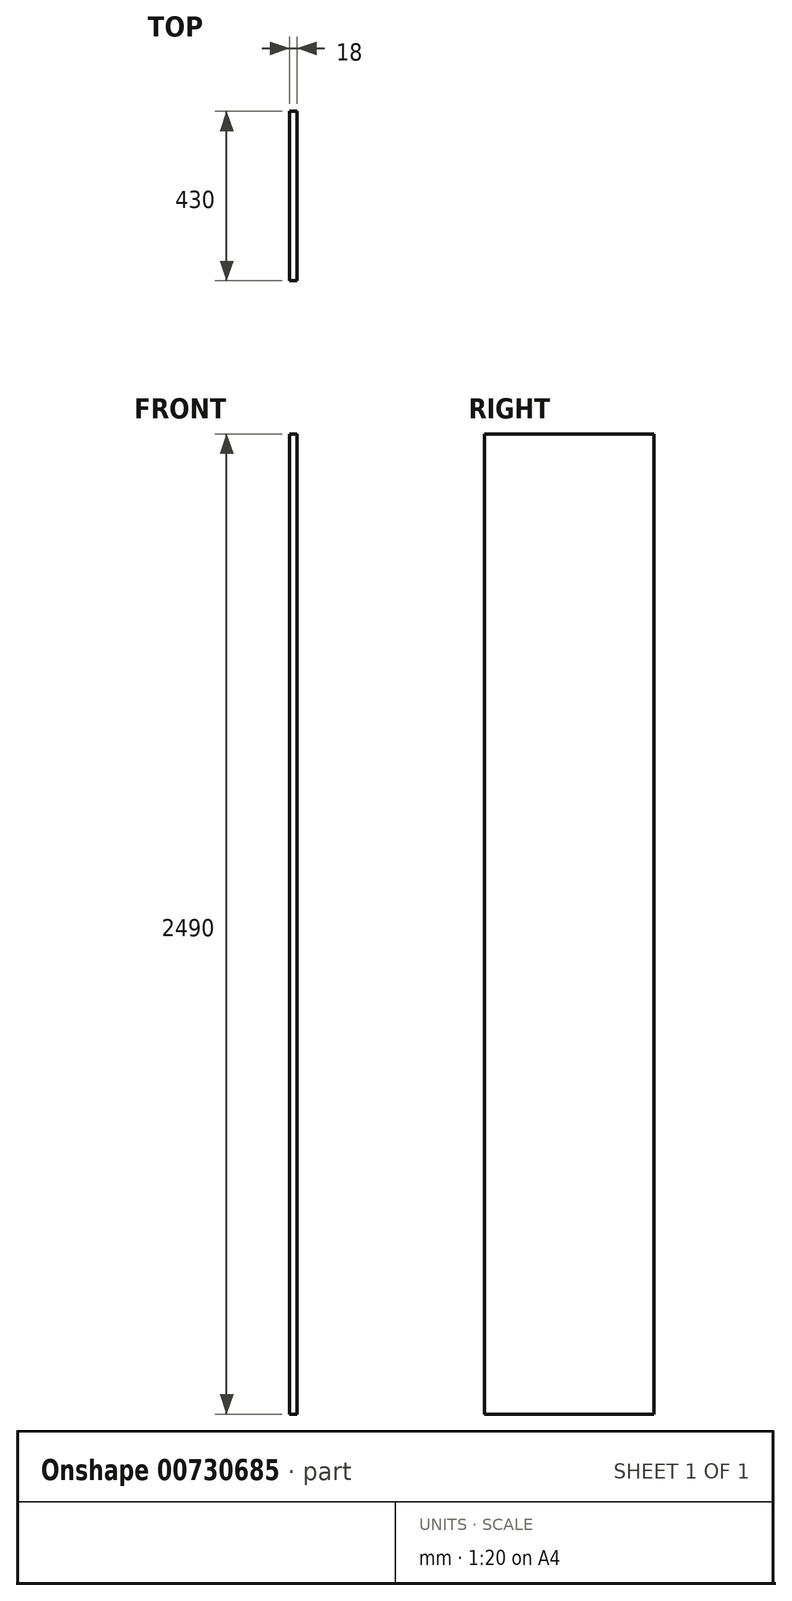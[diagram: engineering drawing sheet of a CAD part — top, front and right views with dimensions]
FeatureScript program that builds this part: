
annotation { "Feature Type Name" : "Feature", "Feature Type Description" : "" }
export const myFeature = defineFeature(function(context is Context, id is Id, definition is map)
    precondition{}
    {
        {
            var Q0;
            Q0=qCreatedBy(makeId("Right.planeOp"),FACE);
            var sketch = newSketch(context, id + "F0", { "sketchPlane" : qUnion([Q0])});
            skLineSegment(sketch, "E0.bottom", {"start": v(0, 0) * mm, "end": v(430, 0) * mm});
            skLineSegment(sketch, "E0.top", {"start": v(0, 2490) * mm, "end": v(430, 2490) * mm});
            skLineSegment(sketch, "E0.left", {"start": v(0, 0) * mm, "end": v(0, 2490) * mm});
            skLineSegment(sketch, "E0.right", {"start": v(430, 0) * mm, "end": v(430, 2490) * mm});
            skSolve(sketch);
        }
        {
            var Q0;
            Q0 = qSketchRegion(id + "F0", true);
            extrude(context, id + "F1", {"entities" : qUnion([Q0]), "depth" : 18 * mm, "offsetDistance" : 25 * mm});
        }
    });
